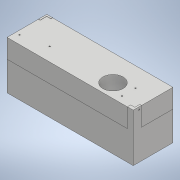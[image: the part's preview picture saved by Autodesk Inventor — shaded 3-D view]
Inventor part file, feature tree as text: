
AUTODESK INVENTOR PART (.ipt)
format: ipt  version: 2020 (Build 240168000, 168)  size: 386,560 bytes
history: native  units: mm
features: sketch x17, other x13, extrude x11, hole x5
ambient origin geometry x8: Origin, YZ Plane, XZ Plane, XY Plane, X Axis, Y Axis, Z Axis, Center Point
bodies: Body1 (feature_tree), Body2 (feature_tree)
feature tree (46):
  other  "Твердое тело1"
  extrude  "Выдавливание1"  Depth=152.5mm
  extrude  "Выдавливание2"  Depth=48.0mm
  extrude  "Выдавливание4"  Depth=30.0mm TaperAngle=0.0deg
  extrude  "Выдавливание7"  Depth=25.0mm
  extrude  "Выдавливание8"  Depth=3.0mm TaperAngle=0.0deg
  extrude  "Выдавливание9"  Depth=2.0mm
  other  "РабПлоскость1"
  other  "Разделение1"
  extrude  "Выдавливание26"  Depth=3.0mm TaperAngle=0.0deg
  extrude  "Выдавливание27"  Depth=24.5mm
  extrude  "Выдавливание28"  Depth=28.0mm
  sketch  "Эскиз24"
  hole  "Отверстие1"  [1 undecoded]
  extrude  "Выдавливание29"  Depth=2.2mm
  hole  "Отверстие2"  [1 undecoded]
  hole  "Отверстие3"  [1 undecoded]
  extrude  "Выдавливание30"  Depth=20.0mm
  hole  "Отверстие4"  [1 undecoded]
  hole  "Отверстие5"  [1 undecoded]
  sketch  "Эскиз1"
  sketch  "Эскиз2"
  sketch  "Эскиз3"
  sketch  "Эскиз4"
  sketch  "Эскиз6"
  sketch  "Эскиз7"
  sketch  "Эскиз20"
  sketch  "Эскиз21"
  sketch  "Эскиз22"
  sketch  "Эскиз23"
  sketch  "Эскиз25"
  sketch  "Эскиз26"
  sketch  "Эскиз27"
  sketch  "Эскиз28"
  sketch  "Эскиз29"
  sketch  "Эскиз30"
  other  "Проецирование ребер1"
  other  "Проецирование ребер3"
  other  "Твердое тело2"
  other  "Твердое тело3"
  other  "Проецирование ребер7"
  other  "Проецирование ребер8"
  other  "Проецирование ребер9"
  other  "Проецирование ребер10"
  other  "Проецирование ребер11"
  other  "Проецирование ребер12"
note: 5 required parameter values undecoded (feature->parameter linkage not recoverable at this tier; creation-order binding heuristic only, values carry confidence <= 0.55)
